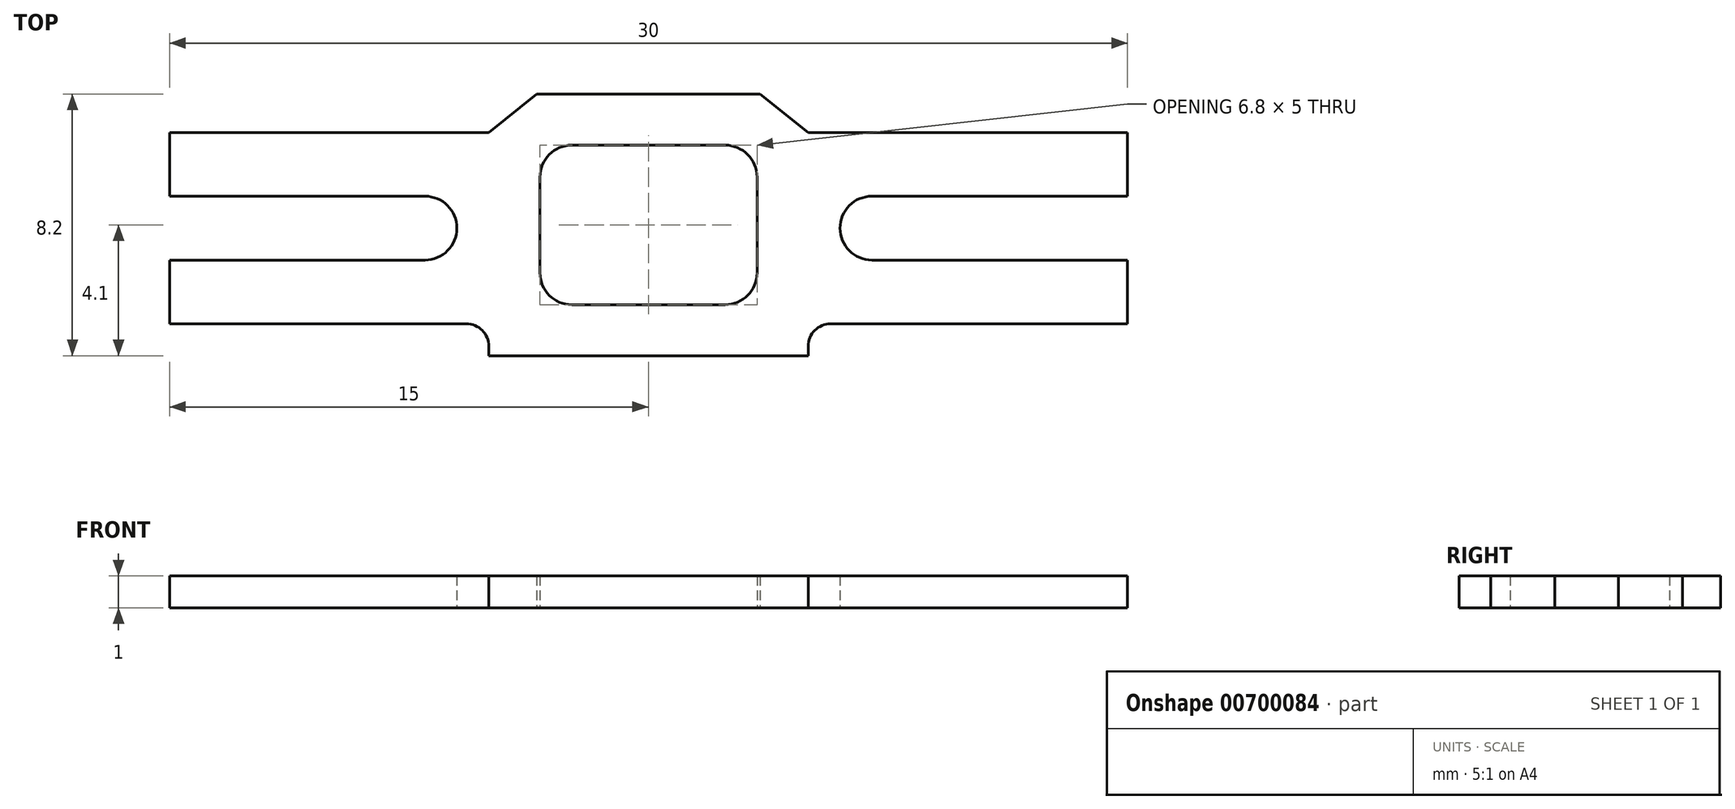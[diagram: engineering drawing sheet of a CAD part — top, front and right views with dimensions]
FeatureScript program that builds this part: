
annotation { "Feature Type Name" : "Feature", "Feature Type Description" : "" }
export const myFeature = defineFeature(function(context is Context, id is Id, definition is map)
    precondition{}
    {
        {
            var Q0;
            Q0=qCreatedBy(makeId("Top.planeOp"),FACE);
            var sketch = newSketch(context, id + "F0", { "sketchPlane" : qUnion([Q0])});
            skLineSegment(sketch, "E0", {"start": v(0, 0) * mm, "end": v(8, 0) * mm});
            skLineSegment(sketch, "E1", {"start": v(8, 0) * mm, "end": v(8, 2) * mm});
            skLineSegment(sketch, "E2", {"start": v(-12, 2) * mm, "end": v(-22, 2) * mm});
            skLineSegment(sketch, "E3", {"start": v(-22, 0) * mm, "end": v(-14, 0) * mm});
            skLineSegment(sketch, "E4", {"start": v(-14, -2) * mm, "end": v(-22, -2) * mm});
            skLineSegment(sketch, "E5", {"start": v(-22, -2) * mm, "end": v(-22, -4) * mm});
            skLineSegment(sketch, "E6", {"start": v(-22, -4) * mm, "end": v(-12.7, -4) * mm});
            skLineSegment(sketch, "E7", {"start": v(-12, -5) * mm, "end": v(-2, -5) * mm});
            skLineSegment(sketch, "E8", {"start": v(-2, -5) * mm, "end": v(-2, -4.7) * mm});
            skLineSegment(sketch, "E9", {"start": v(-1.3, -4) * mm, "end": v(8, -4) * mm});
            skLineSegment(sketch, "E10", {"start": v(8, -4) * mm, "end": v(8, -2) * mm});
            skLineSegment(sketch, "E11", {"start": v(8, -2) * mm, "end": v(0, -2) * mm});
            skLineSegment(sketch, "E12", {"start": v(8, 2) * mm, "end": v(-2, 2) * mm});
            skLineSegment(sketch, "E13", {"start": v(-22, 0) * mm, "end": v(-22, 2) * mm});
            skArc(sketch, "E14", {"start": v(-14, -2) * mm, "mid": v(-13, -1) * mm, "end": v(-14, 0) * mm});
            skArc(sketch, "E15", {"start": v(0, -2) * mm, "mid": v(-1, -1) * mm, "end": v(0, 0) * mm});
            skLineSegment(sketch, "E16", {"start": v(-12, -5) * mm, "end": v(-12, -4.7) * mm});
            skLineSegment(sketch, "E17", {"start": v(-10.5, 3.2) * mm, "end": v(-3.5, 3.2) * mm});
            skLineSegment(sketch, "E18", {"start": v(-12, 2) * mm, "end": v(-10.5, 3.2) * mm});
            skLineSegment(sketch, "E19", {"start": v(-3.5, 3.2) * mm, "end": v(-2, 2) * mm});
            skLineSegment(sketch, "E20", {"start": v(-9.4, -3.4) * mm, "end": v(-4.6, -3.4) * mm});
            skLineSegment(sketch, "E21", {"start": v(-10.4, -2.4) * mm, "end": v(-10.4, 0.6) * mm});
            skLineSegment(sketch, "E22", {"start": v(-3.6, -2.4) * mm, "end": v(-3.6, 0.6) * mm});
            skLineSegment(sketch, "E23", {"start": v(-9.4, 1.6) * mm, "end": v(-4.6, 1.6) * mm});
            skArc(sketch, "E24.filletArc", {"start": v(-9.4, 1.6) * mm, "mid": v(-10.1, 1.3) * mm, "end": v(-10.4, 0.6) * mm});
            skArc(sketch, "E25.filletArc", {"start": v(-3.6, 0.6) * mm, "mid": v(-3.9, 1.3) * mm, "end": v(-4.6, 1.6) * mm});
            skPoint(sketch, "E26.visualSharp", {"position": v(-10.4, -3.4) * mm});
            skArc(sketch, "E26.filletArc", {"start": v(-10.4, -2.4) * mm, "mid": v(-10.1, -3.1) * mm, "end": v(-9.4, -3.4) * mm});
            skPoint(sketch, "E27.visualSharp", {"position": v(-3.6, -3.4) * mm});
            skArc(sketch, "E27.filletArc", {"start": v(-4.6, -3.4) * mm, "mid": v(-3.9, -3.1) * mm, "end": v(-3.6, -2.4) * mm});
            skPoint(sketch, "E28.visualSharp", {"position": v(-12, -4) * mm});
            skArc(sketch, "E28.filletArc", {"start": v(-12, -4.7) * mm, "mid": v(-12.2, -4.2) * mm, "end": v(-12.7, -4) * mm});
            skPoint(sketch, "E29.visualSharp", {"position": v(-2, -4) * mm});
            skArc(sketch, "E29.filletArc", {"start": v(-1.3, -4) * mm, "mid": v(-1.8, -4.2) * mm, "end": v(-2, -4.7) * mm});
            skSolve(sketch);
        }
        {
            var Q0;
            Q0=makeQuery(id+"F0.imprint","IMPRINT",FACE,{"disambiguationData":[TD([[makeQuery(id+"F0.imprint","IMPRINT",EDGE,{"derivedFrom":sQuery(id+"F0.wireOp",EDGE,"E0")}),1.0]])]});
            extrude(context, id + "F1", {"entities" : qUnion([Q0]), "depth" : 1 * mm, "offsetDistance" : 25 * mm});
        }
    });
